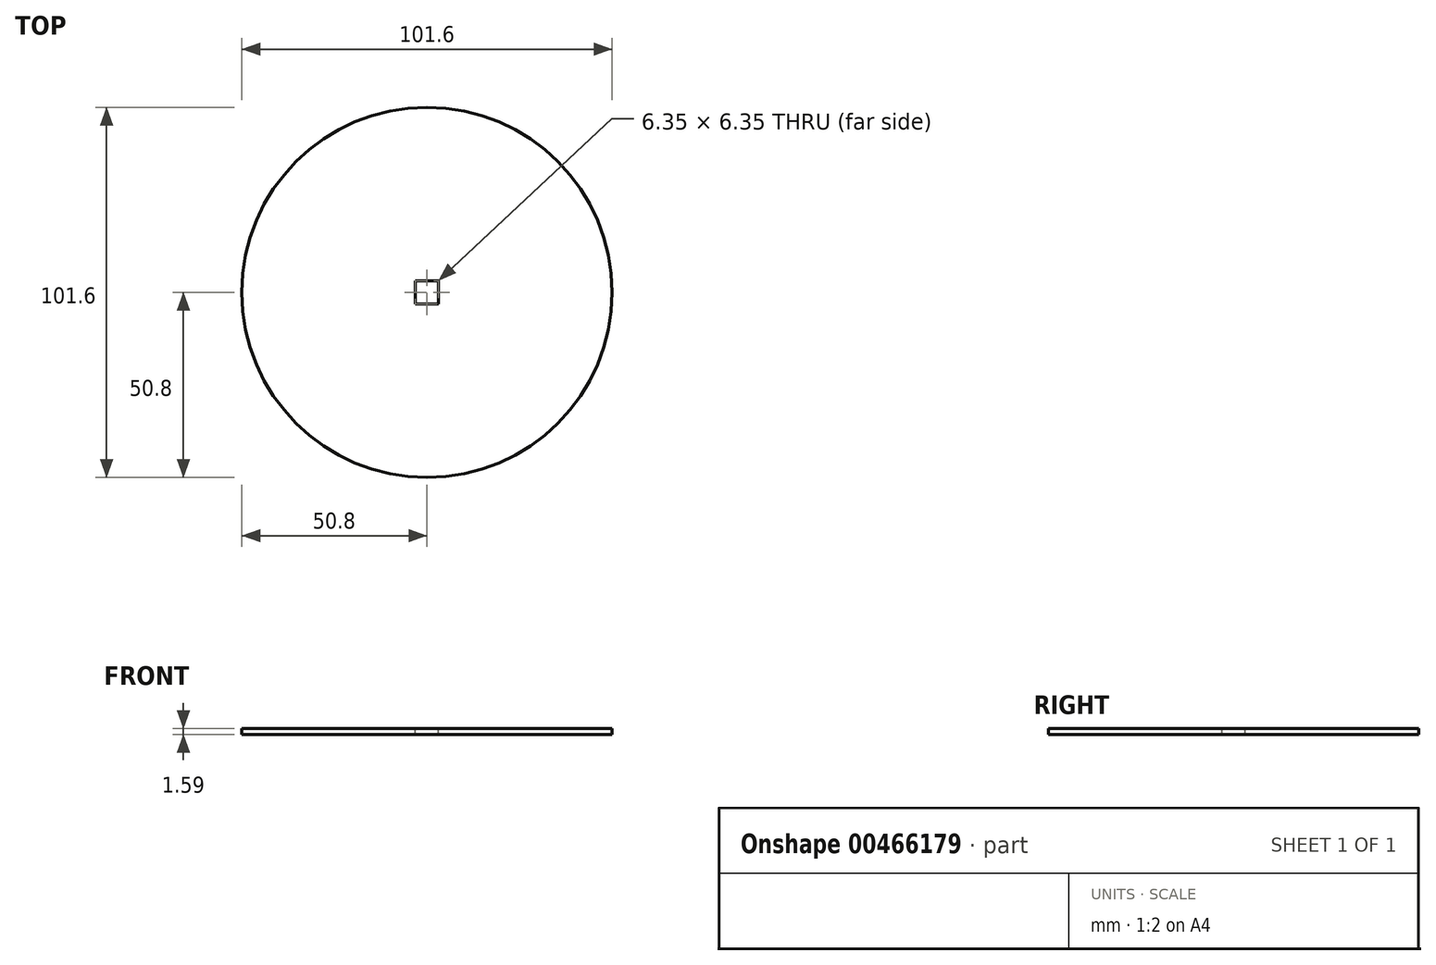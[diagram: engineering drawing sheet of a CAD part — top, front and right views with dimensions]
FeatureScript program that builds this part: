
annotation { "Feature Type Name" : "Feature", "Feature Type Description" : "" }
export const myFeature = defineFeature(function(context is Context, id is Id, definition is map)
    precondition{}
    {
        {
            var Q0;
            Q0=qCreatedBy(makeId("Top.planeOp"),FACE);
            var sketch = newSketch(context, id + "F0", { "sketchPlane" : qUnion([Q0])});
            skCircle(sketch, "E0", {"center": v(0, 0) * mm, "radius": 50.8 * mm});
            skSolve(sketch);
        }
        {
            var Q0;
            Q0=makeQuery(id+"F0.imprint","IMPRINT",FACE,{"disambiguationData":[TD([[makeQuery(id+"F0.imprint","IMPRINT",EDGE,{"derivedFrom":sQuery(id+"F0.wireOp",EDGE,"E0")}),1.0]])]});
            extrude(context, id + "F1", {"entities" : qUnion([Q0]), "depth" : 1.59 * mm});
        }
        {
            var Q0;
            Q0=makeQuery(id+"F1.opExtrude","CAP_FACE",FACE,{"disambiguationData":[OSD([sQuery(id+"F0.wireOp",EDGE,"E0")])],"isStart":false});
            var sketch = newSketch(context, id + "F2", { "sketchPlane" : qUnion([Q0])});
            skLineSegment(sketch, "E1.bottom", {"start": v(3.18, 3.18) * mm, "end": v(-3.18, 3.18) * mm});
            skLineSegment(sketch, "E1.top", {"start": v(3.18, -3.18) * mm, "end": v(-3.18, -3.18) * mm});
            skLineSegment(sketch, "E1.left", {"start": v(3.18, 3.18) * mm, "end": v(3.18, -3.18) * mm});
            skLineSegment(sketch, "E1.right", {"start": v(-3.18, 3.18) * mm, "end": v(-3.18, -3.18) * mm});
            skPoint(sketch, "E1.middle", {"position": v(0, 0) * mm});
            skSolve(sketch);
        }
        {
            var Q0;
            Q0=makeQuery(id+"F2.imprint","IMPRINT",FACE,{"disambiguationData":[TD([[makeQuery(id+"F2.imprint","IMPRINT",EDGE,{"derivedFrom":sQuery(id+"F2.wireOp",EDGE,"E1.bottom")}),1.0]])]});
            extrude(context, id + "F3", {"entities" : qUnion([Q0]), "operationType" : NewBodyOperationType.REMOVE, "oppositeDirection" : true, "depth" : 1.59 * mm});
        }
    });
